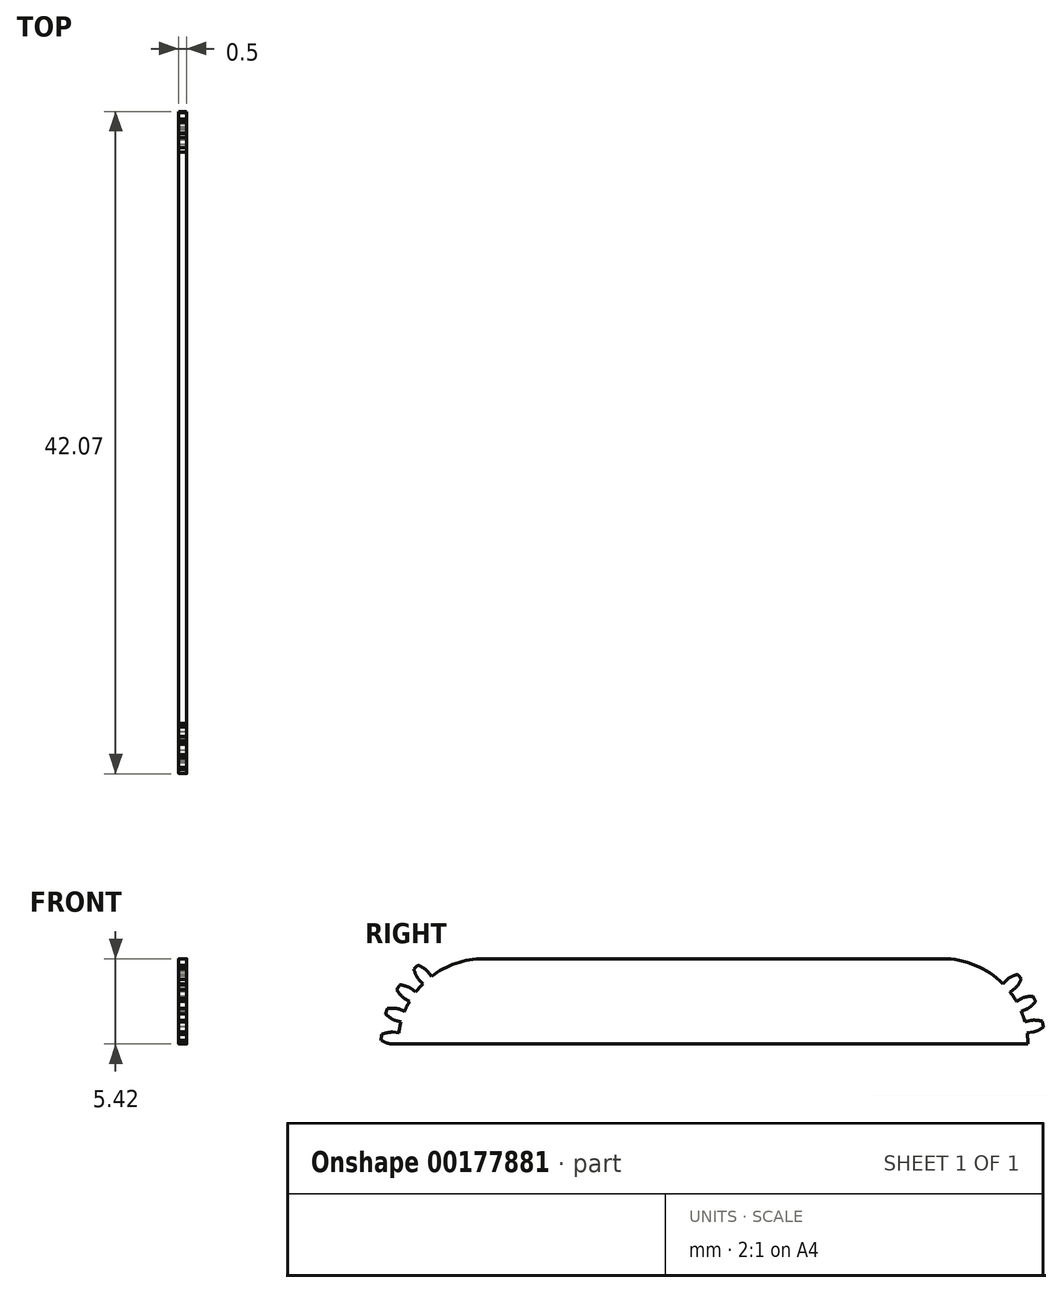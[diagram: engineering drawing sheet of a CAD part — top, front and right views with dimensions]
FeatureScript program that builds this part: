
annotation { "Feature Type Name" : "Feature", "Feature Type Description" : "" }
export const myFeature = defineFeature(function(context is Context, id is Id, definition is map)
    precondition{}
    {
        {
            assignVariable(context, id + "F0", {"name" : "NumberTeeth", "anyValue" : 24});
        }
        {
            assignVariable(context, id + "F1", {"name" : "GearThickness", "anyValue" : .5});
        }
        {
            assignVariable(context, id + "F2", {"name" : "GearToothSpacing", "anyValue" : 360 * degree / getVariable(context, 'NumberTeeth')});
        }
        {
            var Q0;
            Q0=qCreatedBy(makeId("Right.planeOp"),FACE);
            var sketch = newSketch(context, id + "F3", { "sketchPlane" : qUnion([Q0])});
            skCircle(sketch, "E0", {"center": v(0, 0) * mm, "radius": 5.42 * mm});
            skCircle(sketch, "E1", {"center": v(0, 0) * mm, "radius": 5.8 * mm, "construction": true});
            skCircle(sketch, "E2", {"center": v(0, 0) * mm, "radius": 6 * mm, "construction": true});
            skCircle(sketch, "E3", {"center": v(0, 0) * mm, "radius": 6.5 * mm});
            skLineSegment(sketch, "E4", {"start": v(0, 0) * mm, "end": v(-5.8, 0) * mm, "construction": true});
            skLineSegment(sketch, "E5.1.0", {"start": v(0, 0) * mm, "end": v(-5.8, 0.3) * mm, "construction": true});
            skLineSegment(sketch, "E5.2.0", {"start": v(0, 0) * mm, "end": v(-5.78, 0.58) * mm, "construction": true});
            skLineSegment(sketch, "E5.3.0", {"start": v(0, 0) * mm, "end": v(-5.74, 0.87) * mm, "construction": true});
            skLineSegment(sketch, "E5.4.0", {"start": v(0, 0) * mm, "end": v(-5.7, 1.15) * mm, "construction": true});
            skLineSegment(sketch, "E5.5.0", {"start": v(0, 0) * mm, "end": v(-5.63, 1.44) * mm, "construction": true});
            skLineSegment(sketch, "E5.6.0", {"start": v(0, 0) * mm, "end": v(-5.55, 1.72) * mm, "construction": true});
            skLineSegment(sketch, "E5.7.0", {"start": v(0, 0) * mm, "end": v(-5.46, 2) * mm, "construction": true});
            skLineSegment(sketch, "E5.8.0", {"start": v(0, 0) * mm, "end": v(-5.35, 2.26) * mm, "construction": true});
            skLineSegment(sketch, "E5.9.0", {"start": v(0, 0) * mm, "end": v(-5.23, 2.53) * mm, "construction": true});
            skLineSegment(sketch, "E5.10.0", {"start": v(0, 0) * mm, "end": v(-5.1, 2.78) * mm, "construction": true});
            skLineSegment(sketch, "E5.11.0", {"start": v(0, 0) * mm, "end": v(-4.95, 3.04) * mm, "construction": true});
            skLineSegment(sketch, "E5.12.0", {"start": v(0, 0) * mm, "end": v(-4.8, 3.28) * mm, "construction": true});
            skLineSegment(sketch, "E5.13.0", {"start": v(0, 0) * mm, "end": v(-4.62, 3.52) * mm, "construction": true});
            skLineSegment(sketch, "E5.14.0", {"start": v(0, 0) * mm, "end": v(-4.44, 3.74) * mm, "construction": true});
            skLineSegment(sketch, "E5.anchor2", {"start": v(0, 0) * mm, "end": v(-4.44, 3.74) * mm, "construction": true});
            skLineSegment(sketch, "E6", {"start": v(-5.8, 0.3) * mm, "end": v(-5.82, 0) * mm, "construction": true});
            skLineSegment(sketch, "E7", {"start": v(-5.78, 0.58) * mm, "end": v(-5.84, 0) * mm, "construction": true});
            skLineSegment(sketch, "E8", {"start": v(-5.74, 0.87) * mm, "end": v(-5.87, 0) * mm, "construction": true});
            skLineSegment(sketch, "E9", {"start": v(-5.63, 1.44) * mm, "end": v(-5.99, 0.03) * mm, "construction": true});
            skLineSegment(sketch, "E10", {"start": v(-5.55, 1.72) * mm, "end": v(-6.06, 0.05) * mm, "construction": true});
            skLineSegment(sketch, "E11", {"start": v(-5.46, 2) * mm, "end": v(-6.15, 0.08) * mm, "construction": true});
            skLineSegment(sketch, "E12", {"start": v(-5.35, 2.26) * mm, "end": v(-6.26, 0.12) * mm, "construction": true});
            skLineSegment(sketch, "E13", {"start": v(-5.23, 2.53) * mm, "end": v(-6.37, 0.17) * mm, "construction": true});
            skLineSegment(sketch, "E14", {"start": v(-5.1, 2.78) * mm, "end": v(-6.5, 0.24) * mm, "construction": true});
            skLineSegment(sketch, "E15", {"start": v(-4.95, 3.04) * mm, "end": v(-6.62, 0.31) * mm, "construction": true});
            skLineSegment(sketch, "E16", {"start": v(-5.7, 1.15) * mm, "end": v(-5.92, 0.02) * mm, "construction": true});
            skLineSegment(sketch, "E17", {"start": v(-4.8, 3.28) * mm, "end": v(-6.76, 0.4) * mm, "construction": true});
            skLineSegment(sketch, "E18", {"start": v(-4.62, 3.52) * mm, "end": v(-6.9, 0.5) * mm, "construction": true});
            skLineSegment(sketch, "E19", {"start": v(-4.44, 3.74) * mm, "end": v(-7.06, 0.63) * mm, "construction": true});
            skLineSegment(sketch, "E20", {"start": v(0, 0) * mm, "end": v(-5.8, 0.38) * mm, "construction": true});
            skLineSegment(sketch, "E21", {"start": v(-5.42, 0) * mm, "end": v(-5.8, 0) * mm});
            skLineSegment(sketch, "E22.MirrorCS", {"start": v(-5.38, 0.7) * mm, "end": v(-5.76, 0.76) * mm});
            skLineSegment(sketch, "E23", {"start": v(-7.06, 0.63) * mm, "end": v(-7.93, 1.36) * mm, "construction": true});
            skFitSpline(sketch, "E24", {"points": [v(-7.06, 0.63) * mm, v(-6.9, 0.5) * mm, v(-6.76, 0.4) * mm, v(-6.62, 0.31) * mm, v(-6.5, 0.24) * mm, v(-6.37, 0.17) * mm, v(-6.26, 0.12) * mm, v(-6.15, 0.08) * mm, v(-6.06, 0.05) * mm, v(-5.99, 0.03) * mm, v(-5.92, 0.02) * mm, v(-5.87, 0) * mm, v(-5.84, 0) * mm, v(-5.82, 0) * mm, v(-5.8, 0) * mm], "startDerivative": vector(0.19, -0.16) * mm, "endDerivative": vector(0.04, 0) * mm});
            skFitSpline(sketch, "E25.MirrorCS", {"points": [v(-7.08, 0.3) * mm, v(-6.92, 0.4) * mm, v(-6.76, 0.48) * mm, v(-6.6, 0.55) * mm, v(-6.47, 0.61) * mm, v(-6.34, 0.66) * mm, v(-6.22, 0.7) * mm, v(-6.11, 0.72) * mm, v(-6.02, 0.74) * mm, v(-5.94, 0.75) * mm, v(-5.88, 0.76) * mm, v(-5.82, 0.76) * mm, v(-5.79, 0.76) * mm, v(-5.77, 0.76) * mm, v(-5.76, 0.76) * mm], "startDerivative": vector(0.2, 0.13) * mm, "endDerivative": vector(0.04, 0) * mm});
            skLineSegment(sketch, "E26", {"start": v(-5.42, 0) * mm, "end": v(34.58, 0) * mm});
            skLineSegment(sketch, "E27", {"start": v(14.58, 0) * mm, "end": v(14.58, 6.8) * mm, "construction": true});
            skLineSegment(sketch, "E28", {"start": v(34.58, 0) * mm, "end": v(34.58, -5.37) * mm, "construction": true});
            skLineSegment(sketch, "E29", {"start": v(0, 5.42) * mm, "end": v(29.16, 5.42) * mm});
            skArc(sketch, "E30", {"start": v(29.16, 5.42) * mm, "mid": v(33, 3.83) * mm, "end": v(34.58, 0) * mm});
            skLineSegment(sketch, "E31.MirrorCS", {"start": v(34.58, 0) * mm, "end": v(34.97, 0) * mm});
            skLineSegment(sketch, "E32.MirrorCS", {"start": v(34.53, 0.7) * mm, "end": v(34.92, 0.76) * mm});
            skFitSpline(sketch, "E33.MirrorCS", {"points": [v(36.24, 0.3) * mm, v(36.07, 0.4) * mm, v(35.91, 0.48) * mm, v(35.76, 0.55) * mm, v(35.62, 0.61) * mm, v(35.5, 0.66) * mm, v(35.37, 0.7) * mm, v(35.27, 0.72) * mm, v(35.18, 0.74) * mm, v(35.1, 0.75) * mm, v(35.03, 0.76) * mm, v(34.98, 0.76) * mm, v(34.95, 0.76) * mm, v(34.92, 0.76) * mm, v(34.92, 0.76) * mm], "startDerivative": vector(-0.2, 0.13) * mm, "endDerivative": vector(-0.04, 0) * mm});
            skFitSpline(sketch, "E34.MirrorCS", {"points": [v(36.22, 0.63) * mm, v(36.07, 0.5) * mm, v(35.92, 0.4) * mm, v(35.78, 0.31) * mm, v(35.65, 0.24) * mm, v(35.52, 0.17) * mm, v(35.41, 0.12) * mm, v(35.31, 0.08) * mm, v(35.22, 0.05) * mm, v(35.14, 0.03) * mm, v(35.08, 0.02) * mm, v(35.03, 0) * mm, v(35, 0) * mm, v(34.97, 0) * mm, v(34.97, 0) * mm], "startDerivative": vector(-0.19, -0.16) * mm, "endDerivative": vector(-0.04, 0) * mm});
            skFitSpline(sketch, "E35.MirrorCS", {"points": [v(36.14, 1.22) * mm, v(35.96, 1.3) * mm, v(35.8, 1.36) * mm, v(35.63, 1.41) * mm, v(35.49, 1.45) * mm, v(35.35, 1.48) * mm, v(35.23, 1.5) * mm, v(35.12, 1.51) * mm, v(35.03, 1.52) * mm, v(34.95, 1.52) * mm, v(34.88, 1.52) * mm, v(34.83, 1.51) * mm, v(34.8, 1.5) * mm, v(34.78, 1.5) * mm, v(34.77, 1.5) * mm], "startDerivative": vector(-0.22, 0.1) * mm, "endDerivative": vector(-0.04, 0) * mm});
            skFitSpline(sketch, "E36.MirrorCS", {"points": [v(36.08, 1.55) * mm, v(35.94, 1.4) * mm, v(35.8, 1.28) * mm, v(35.68, 1.17) * mm, v(35.56, 1.08) * mm, v(35.45, 1) * mm, v(35.34, 0.94) * mm, v(35.25, 0.88) * mm, v(35.16, 0.84) * mm, v(35.09, 0.81) * mm, v(35.03, 0.79) * mm, v(34.98, 0.77) * mm, v(34.94, 0.76) * mm, v(34.92, 0.76) * mm, v(34.92, 0.76) * mm], "startDerivative": vector(-0.17, -0.18) * mm, "endDerivative": vector(-0.04, 0) * mm});
            skLineSegment(sketch, "E37.MirrorCS", {"start": v(34.4, 1.4) * mm, "end": v(34.77, 1.5) * mm});
            skCircle(sketch, "E38.MirrorC", {"center": v(29.16, 0) * mm, "radius": 6.5 * mm});
            skSolve(sketch);
        }
        {
            var Q0;
            {var subQ0=sQuery(id+"F3.wireOp",EDGE,"E0");var subQ1=makeQuery(id+"F3.imprint","INTERSECT",VERTEX,{"derivedFrom":[subQ0,sQuery(id+"F3.wireOp",EDGE,"E21")]});Q0=makeQuery(id+"F3.imprint","IMPRINT",FACE,{"disambiguationData":[TD([[makeQuery(id+"F3.imprint","IMPRINT",EDGE,{"disambiguationData":[TD([[subQ1,1.0]])],"derivedFrom":subQ0}),1.0]])]});}
            var Q1;
            {var subQ1=sQuery(id+"F3.wireOp",EDGE,"E29");var subQ3=sQuery(id+"F3.wireOp",EDGE,"E3");var subQ4=makeQuery(id+"F3.imprint","INTERSECT",VERTEX,{"derivedFrom":[subQ3,subQ1]});Q1=makeQuery(id+"F3.imprint","IMPRINT",FACE,{"disambiguationData":[TD([[makeQuery(id+"F3.imprint","IMPRINT",EDGE,{"disambiguationData":[TD([[subQ4,1.0]])],"derivedFrom":subQ3}),-1.0]])]});}
            var Q2;
            {var subQ0=sQuery(id+"F3.wireOp",EDGE,"E29");var subQ1=sQuery(id+"F3.wireOp",EDGE,"E0");var subQ2=makeQuery(id+"F3.imprint","INTERSECT",VERTEX,{"derivedFrom":[subQ1,subQ0]});Q2=makeQuery(id+"F3.imprint","IMPRINT",FACE,{"disambiguationData":[TD([[makeQuery(id+"F3.imprint","IMPRINT",EDGE,{"disambiguationData":[TD([[subQ2,1.0]])],"derivedFrom":subQ1}),-1.0]])]});}
            var Q3;
            {var subQ0=sQuery(id+"F3.wireOp",EDGE,"E30");var subQ5=sQuery(id+"F3.wireOp",EDGE,"E29");var subQ6=makeQuery(id+"F3.imprint","INTERSECT",VERTEX,{"derivedFrom":[subQ5,subQ0]});Q3=makeQuery(id+"F3.imprint","IMPRINT",FACE,{"disambiguationData":[TD([[makeQuery(id+"F3.imprint","IMPRINT",EDGE,{"disambiguationData":[TD([[subQ6,1.0]])],"derivedFrom":subQ5}),-1.0]])]});}
            extrude(context, id + "F4", {"entities" : qUnion([Q0, Q1, Q2, Q3]), "depth" : (getVariable(context, 'GearThickness')) * mm});
        }
        {
            var Q0;
            {var subQ1=sQuery(id+"F3.wireOp",EDGE,"E21");Q0=makeQuery(id+"F3.imprint","IMPRINT",FACE,{"disambiguationData":[TD([[makeQuery(id+"F3.imprint","IMPRINT",EDGE,{"derivedFrom":subQ1}),-1.0]])]});}
            var Q1;
            {var subQ1=sQuery(id+"F3.wireOp",EDGE,"E32.MirrorCS");Q1=makeQuery(id+"F3.imprint","IMPRINT",FACE,{"disambiguationData":[TD([[makeQuery(id+"F3.imprint","IMPRINT",EDGE,{"derivedFrom":subQ1}),1.0]])]});}
            extrude(context, id + "F5", {"entities" : qUnion([Q0, Q1]), "depth" : (getVariable(context, 'GearThickness')) * mm});
        }
        {
            var Q0;
            Q0=makeQuery(id+"F5.opExtrude","SWEPT_BODY",BODY,{"disambiguationData":[OSD([sQuery(id+"F3.wireOp",EDGE,"E0"),sQuery(id+"F3.wireOp",EDGE,"E3"),sQuery(id+"F3.wireOp",EDGE,"E21"),sQuery(id+"F3.wireOp",EDGE,"E22.MirrorCS"),sQuery(id+"F3.wireOp",EDGE,"E24"),sQuery(id+"F3.wireOp",EDGE,"E25.MirrorCS")])]});
            var Q1;
            Q1=makeQuery(id+"F4.opExtrude","SWEPT_FACE",FACE,{"disambiguationData":[OSD([sQuery(id+"F3.wireOp",EDGE,"abc1c1ef-9107-4900-9671-dac890a315ee0.MirrorCS")])]});
            var Q2;
            Q2=makeQuery(id+"F4.opExtrude","SWEPT_FACE",FACE,{"disambiguationData":[OSD([sQuery(id+"F3.wireOp",EDGE,"33001111-3cf2-4703-a9ad-cefdc3e51004")])]});
            var Q3;
            Q3=makeQuery(id+"F4.opExtrude","SWEPT_FACE",FACE,{"disambiguationData":[OSD([sQuery(id+"F3.wireOp",EDGE,"E3")])]});
            var Q4;
            Q4=makeQuery(id+"F4.opExtrude","SWEPT_FACE",FACE,{"disambiguationData":[OSD([sQuery(id+"F3.wireOp",EDGE,"E22.MirrorCS")])]});
            var Q5;
            Q5=makeQuery(id+"F4.opExtrude","SWEPT_FACE",FACE,{"disambiguationData":[OSD([sQuery(id+"F3.wireOp",EDGE,"E21")])]});
            var Q6;
            Q6=makeQuery(id+"F4.opExtrude","SWEPT_FACE",FACE,{"disambiguationData":[OSD([sQuery(id+"F3.wireOp",EDGE,"E0")])]});
            circularPattern(context, id + "F6", {"operationType" : NewBodyOperationType.ADD, "entities" : qUnion([Q0]), "axis" : qUnion([Q6]), "angle" : getVariable(context, 'GearToothSpacing'), "instanceCount" : 4});
        }
        {
            var Q0;
            Q0=makeQuery(id+"F5.opExtrude","SWEPT_BODY",BODY,{"disambiguationData":[OSD([sQuery(id+"F3.wireOp",EDGE,"E30"),sQuery(id+"F3.wireOp",EDGE,"E32.MirrorCS"),sQuery(id+"F3.wireOp",EDGE,"E35.MirrorCS"),sQuery(id+"F3.wireOp",EDGE,"E36.MirrorCS"),sQuery(id+"F3.wireOp",EDGE,"E37.MirrorCS")])]});
            var Q1;
            Q1=makeQuery(id+"F4.opExtrude","SWEPT_FACE",FACE,{"disambiguationData":[OSD([sQuery(id+"F3.wireOp",EDGE,"E30")])]});
            circularPattern(context, id + "F7", {"operationType" : NewBodyOperationType.ADD, "entities" : qUnion([Q0]), "axis" : qUnion([Q1]), "angle" : getVariable(context, 'GearToothSpacing'), "instanceCount" : 3, "oppositeDirection" : true});
        }
    });
